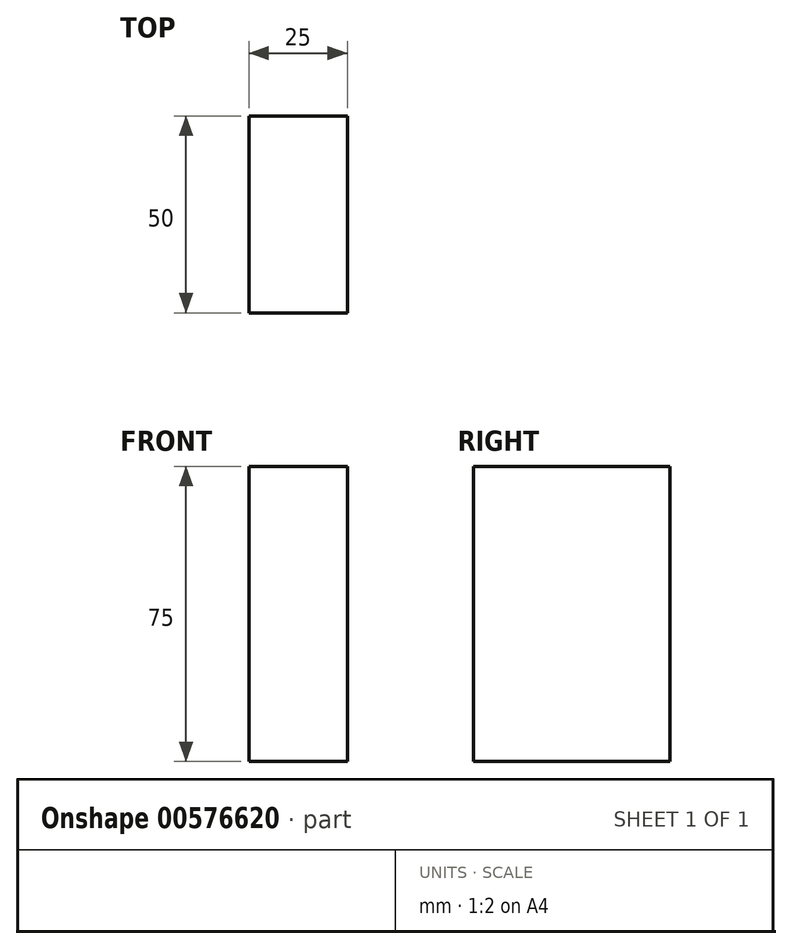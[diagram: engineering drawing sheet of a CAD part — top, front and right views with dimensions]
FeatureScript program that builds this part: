
annotation { "Feature Type Name" : "Feature", "Feature Type Description" : "" }
export const myFeature = defineFeature(function(context is Context, id is Id, definition is map)
    precondition{}
    {
        {
            var Q0;
            Q0=qCreatedBy(makeId("Top.planeOp"),FACE);
            var sketch = newSketch(context, id + "F0", { "sketchPlane" : qUnion([Q0])});
            skLineSegment(sketch, "E0.bottom", {"start": v(0, 0) * mm, "end": v(25, 0) * mm});
            skLineSegment(sketch, "E0.top", {"start": v(0, 50) * mm, "end": v(25, 50) * mm});
            skLineSegment(sketch, "E0.left", {"start": v(0, 0) * mm, "end": v(0, 50) * mm});
            skLineSegment(sketch, "E0.right", {"start": v(25, 0) * mm, "end": v(25, 50) * mm});
            skSolve(sketch);
        }
        {
            var Q0;
            Q0=makeQuery(id+"F0.imprint","IMPRINT",FACE,{"disambiguationData":[TD([[makeQuery(id+"F0.imprint","IMPRINT",EDGE,{"derivedFrom":sQuery(id+"F0.wireOp",EDGE,"E0.bottom")}),1.0]])]});
            var Q1;
            Q1=makeQuery(id+"F0.imprint","IMPRINT",FACE,{"disambiguationData":[TD([[makeQuery(id+"F0.imprint","IMPRINT",EDGE,{"derivedFrom":sQuery(id+"F0.wireOp",EDGE,"E0.bottom")}),1.0]])]});
            extrude(context, id + "F1", {"entities" : qUnion([Q0, Q1]), "depth" : 75 * mm, "offsetDistance" : 25 * mm});
        }
    });
